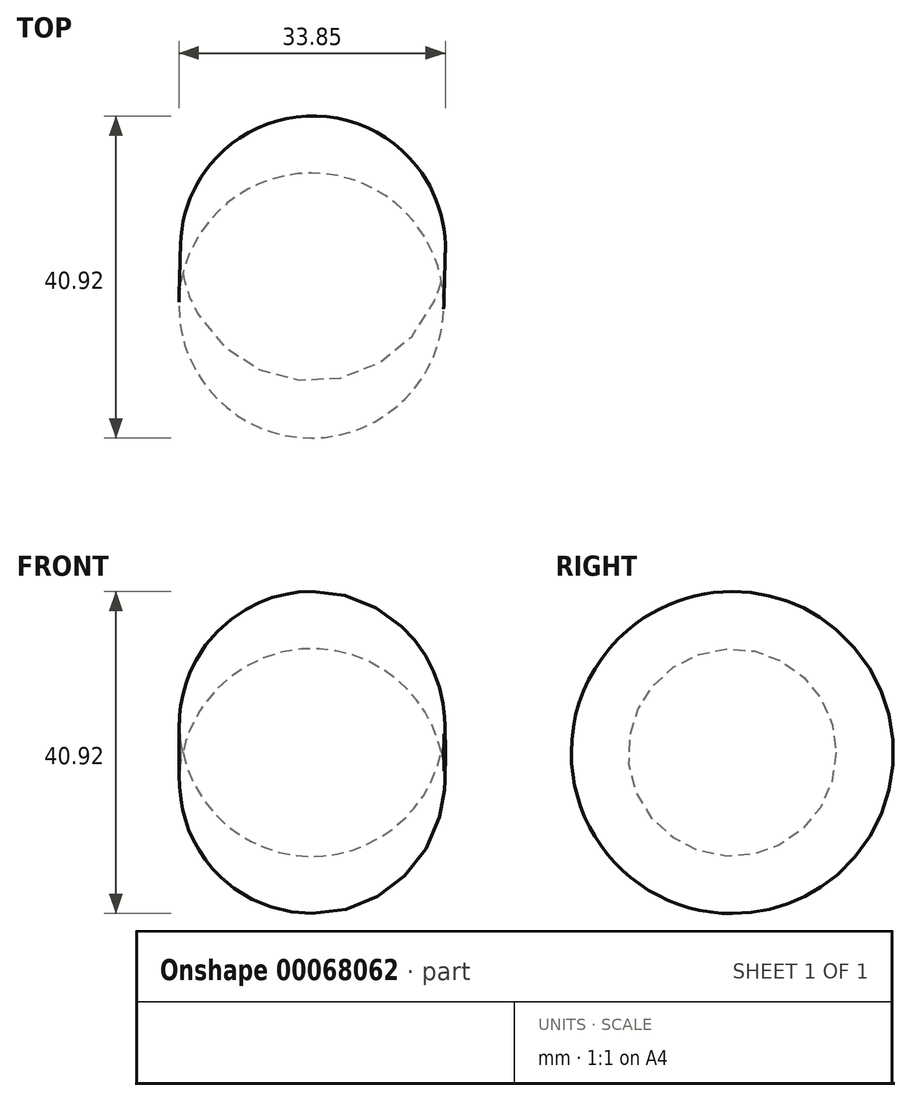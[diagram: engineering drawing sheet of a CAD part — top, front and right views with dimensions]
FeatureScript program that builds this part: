
annotation { "Feature Type Name" : "Feature", "Feature Type Description" : "" }
export const myFeature = defineFeature(function(context is Context, id is Id, definition is map)
    precondition{}
    {
        {
            var Q0;
            Q0=qCreatedBy(makeId("Top.planeOp"),FACE);
            var sketch = newSketch(context, id + "F0", { "sketchPlane" : qUnion([Q0])});
            skArc(sketch, "E0", {"start": v(-21.11, 37) * mm, "mid": v(-37.17, 50.63) * mm, "end": v(-53.95, 37.9) * mm});
            skLineSegment(sketch, "E1", {"start": v(-53.95, 37.9) * mm, "end": v(-21.11, 37) * mm});
            skSolve(sketch);
        }
        {
            var Q0;
            Q0 = qSketchRegion(id + "F0", true);
            var Q1;
            Q1=sQuery(id+"F0.wireOp",EDGE,"E1");
            revolve(context, id + "F1", {"entities" : qUnion([Q0]), "axis" : qUnion([Q1]), "revolveType" : RevolveType.FULL});
        }
    });
